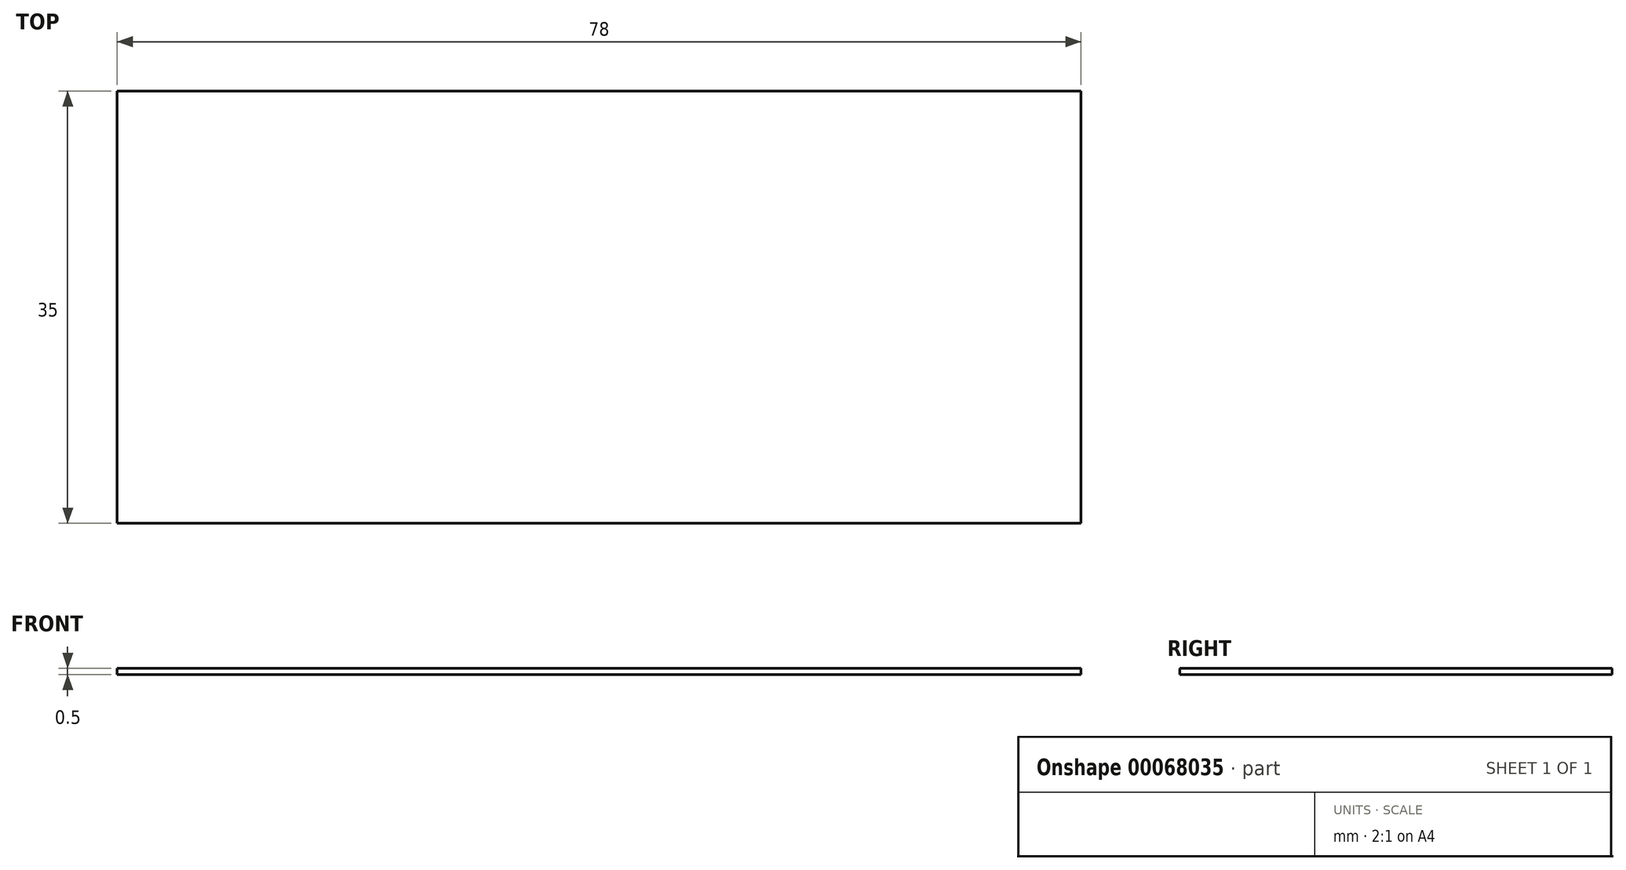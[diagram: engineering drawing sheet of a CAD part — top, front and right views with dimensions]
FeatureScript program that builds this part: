
annotation { "Feature Type Name" : "Feature", "Feature Type Description" : "" }
export const myFeature = defineFeature(function(context is Context, id is Id, definition is map)
    precondition{}
    {
        {
            var Q0;
            Q0=qCreatedBy(makeId("Top.planeOp"),FACE);
            var sketch = newSketch(context, id + "F0", { "sketchPlane" : qUnion([Q0])});
            skLineSegment(sketch, "E0.bottom", {"start": v(0, 0) * mm, "end": v(78, 0) * mm});
            skLineSegment(sketch, "E0.top", {"start": v(0, 35) * mm, "end": v(78, 35) * mm});
            skLineSegment(sketch, "E0.left", {"start": v(0, 0) * mm, "end": v(0, 35) * mm});
            skLineSegment(sketch, "E0.right", {"start": v(78, 0) * mm, "end": v(78, 35) * mm});
            skSolve(sketch);
        }
        {
            var Q0;
            Q0=makeQuery(id+"F0.imprint","IMPRINT",FACE,{"disambiguationData":[TD([[makeQuery(id+"F0.imprint","IMPRINT",EDGE,{"derivedFrom":sQuery(id+"F0.wireOp",EDGE,"E0.bottom")}),1.0]])]});
            extrude(context, id + "F1", {"entities" : qUnion([Q0]), "depth" : 0.5 * mm});
        }
    });
